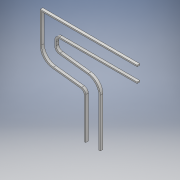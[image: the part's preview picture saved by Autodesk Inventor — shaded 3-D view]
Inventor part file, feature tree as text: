
AUTODESK INVENTOR PART (.ipt)
format: ipt  version: 2017 (Build 210142000, 142)  size: 173,056 bytes
history: native  units: mm
features: fillet x5, extrude x1, sketch x1
ambient origin geometry x8: Origin, YZ Plane, XZ Plane, XY Plane, X Axis, Y Axis, Z Axis, Center Point
bodies: Solide1 (feature_tree)
feature tree (7):
  extrude  "Extrusion1"  Depth=146.0mm
  fillet  "Congé7"  Radius=90.0mm
  fillet  "Congé9"  Radius=10.0mm
  fillet  "Congé10"  Radius=3.0mm
  fillet  "Congé11"  Radius=6.0mm
  fillet  "Congé12"  Radius=30.0mm
  sketch  "Esquisse1"
